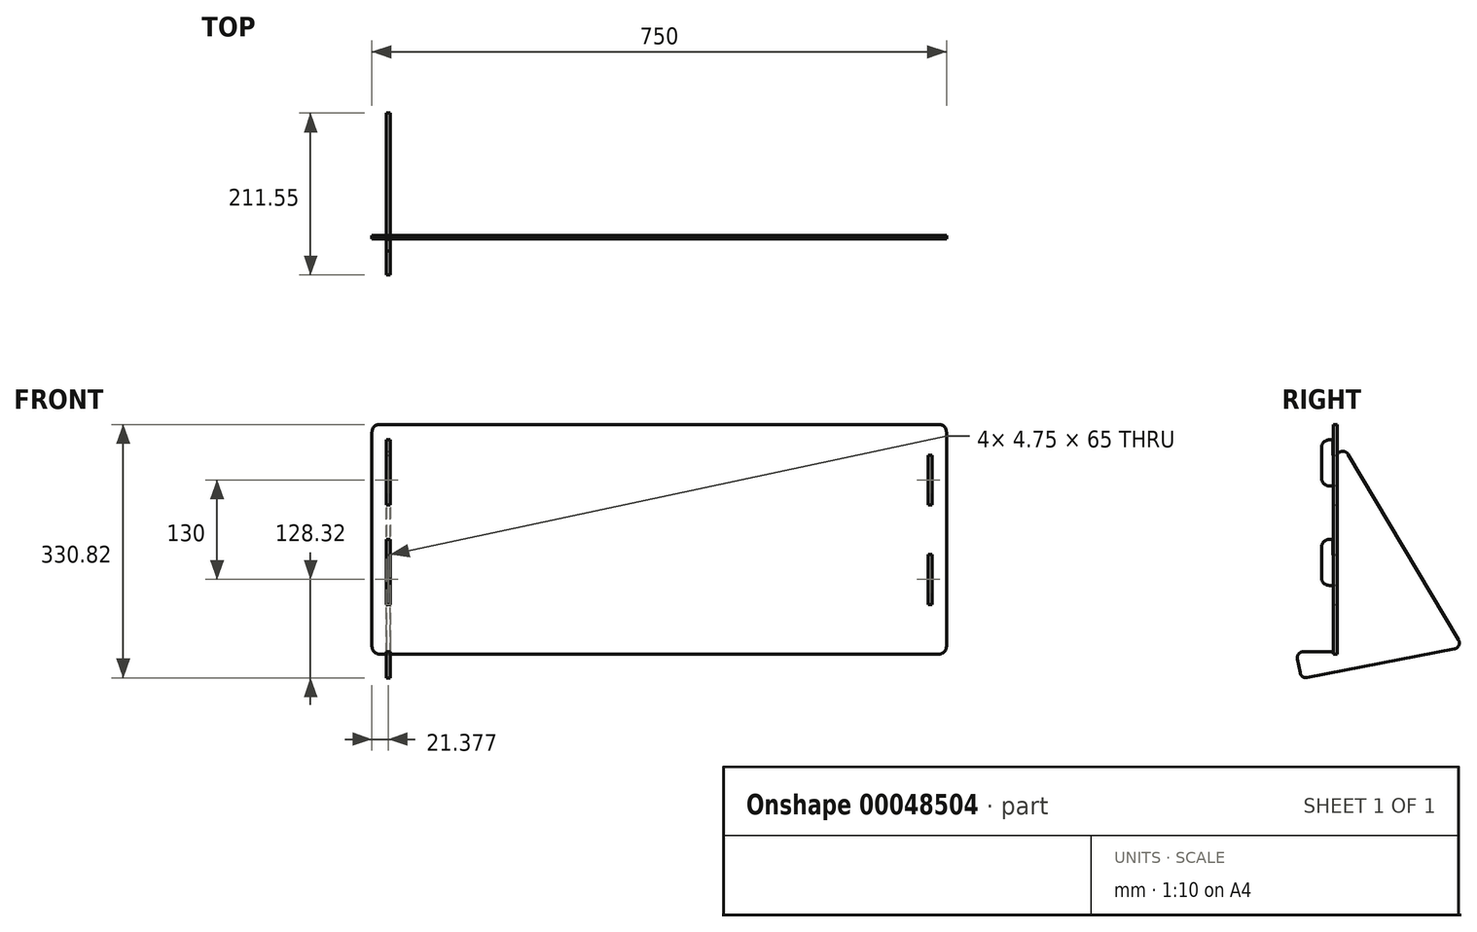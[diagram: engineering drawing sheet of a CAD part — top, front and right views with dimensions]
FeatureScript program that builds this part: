
annotation { "Feature Type Name" : "Feature", "Feature Type Description" : "" }
export const myFeature = defineFeature(function(context is Context, id is Id, definition is map)
    precondition{}
    {
        {
            assignVariable(context, id + "F0", {"name" : "thick", "anyValue" : 4.75});
        }
        {
            var Q0;
            Q0=qCreatedBy(makeId("Front.planeOp"),FACE);
            var sketch = newSketch(context, id + "F1", { "sketchPlane" : qUnion([Q0])});
            skLineSegment(sketch, "E0.bottom", {"start": v(-809.9, 170) * mm, "end": v(-59.9, 170) * mm});
            skLineSegment(sketch, "E0.top", {"start": v(-809.9, -130) * mm, "end": v(-59.9, -130) * mm});
            skLineSegment(sketch, "E0.left", {"start": v(-809.9, 170) * mm, "end": v(-809.9, -130) * mm});
            skLineSegment(sketch, "E0.right", {"start": v(-59.9, 170) * mm, "end": v(-59.9, -130) * mm});
            skLineSegment(sketch, "E1.bottom", {"start": v(-790.9, 130) * mm, "end": v(-786.16, 130) * mm});
            skLineSegment(sketch, "E1.top", {"start": v(-790.9, 65) * mm, "end": v(-786.16, 65) * mm});
            skLineSegment(sketch, "E1.left", {"start": v(-790.9, 130) * mm, "end": v(-790.9, 65) * mm});
            skLineSegment(sketch, "E1.right", {"start": v(-786.16, 130) * mm, "end": v(-786.16, 65) * mm});
            skLineSegment(sketch, "E2.bottom", {"start": v(-790.9, 0) * mm, "end": v(-786.16, 0) * mm});
            skLineSegment(sketch, "E2.top", {"start": v(-790.9, -65) * mm, "end": v(-786.16, -65) * mm});
            skLineSegment(sketch, "E2.left", {"start": v(-790.9, 0) * mm, "end": v(-790.9, -65) * mm});
            skLineSegment(sketch, "E2.right", {"start": v(-786.16, 0) * mm, "end": v(-786.16, -65) * mm});
            skLineSegment(sketch, "E3", {"start": v(-434.9, 170) * mm, "end": v(-434.9, -130) * mm, "construction": true});
            skLineSegment(sketch, "E4.MirrorCS", {"start": v(-78.9, -65) * mm, "end": v(-83.66, -65) * mm});
            skLineSegment(sketch, "E5.MirrorCS", {"start": v(-78.9, 65) * mm, "end": v(-83.66, 65) * mm});
            skLineSegment(sketch, "E6.MirrorCS", {"start": v(-78.9, 130) * mm, "end": v(-83.66, 130) * mm});
            skLineSegment(sketch, "E7.MirrorCS", {"start": v(-78.9, 0) * mm, "end": v(-83.66, 0) * mm});
            skLineSegment(sketch, "E8.MirrorCS", {"start": v(-78.9, 0) * mm, "end": v(-78.9, -65) * mm});
            skLineSegment(sketch, "E9.MirrorCS", {"start": v(-83.66, 130) * mm, "end": v(-83.66, 65) * mm});
            skLineSegment(sketch, "E10.MirrorCS", {"start": v(-78.9, 130) * mm, "end": v(-78.9, 65) * mm});
            skLineSegment(sketch, "E11.MirrorCS", {"start": v(-83.66, 0) * mm, "end": v(-83.66, -65) * mm});
            skSolve(sketch);
        }
        {
            var Q0;
            Q0=makeQuery(id+"F1.imprint","IMPRINT",FACE,{"disambiguationData":[TD([[makeQuery(id+"F1.imprint","IMPRINT",EDGE,{"derivedFrom":sQuery(id+"F1.wireOp",EDGE,"E0.bottom")}),-1.0]])]});
            extrude(context, id + "F2", {"entities" : qUnion([Q0]), "depth" : (getVariable(context, 'thick')) * mm});
        }
        {
            var Q0;
            Q0=makeQuery(id+"F2.opExtrude","SWEPT_FACE",FACE,{"disambiguationData":[OSD([sQuery(id+"F1.wireOp",EDGE,"E1.right")])]});
            var sketch = newSketch(context, id + "F3", { "sketchPlane" : qUnion([Q0])});
            skLineSegment(sketch, "E12", {"start": v(5.25, 149.79) * mm, "end": v(5.25, 129.79) * mm});
            skLineSegment(sketch, "E13", {"start": v(5.25, 129.79) * mm, "end": v(0, 129.79) * mm});
            skLineSegment(sketch, "E14", {"start": v(0, 129.79) * mm, "end": v(0, 155.14) * mm});
            skLineSegment(sketch, "E15", {"start": v(0, 155.14) * mm, "end": v(-164.33, -121.03) * mm});
            skLineSegment(sketch, "E16", {"start": v(0, -130.21) * mm, "end": v(0, -40.21) * mm});
            skLineSegment(sketch, "E17", {"start": v(0, -40.21) * mm, "end": v(20.25, -40.21) * mm});
            skLineSegment(sketch, "E18", {"start": v(20.25, -40.21) * mm, "end": v(20.25, 19.79) * mm});
            skLineSegment(sketch, "E19", {"start": v(5.25, 19.79) * mm, "end": v(20.25, 19.79) * mm});
            skLineSegment(sketch, "E20", {"start": v(5.25, 19.79) * mm, "end": v(5.25, -0.21) * mm});
            skLineSegment(sketch, "E21", {"start": v(5.25, -0.21) * mm, "end": v(0, -0.21) * mm});
            skLineSegment(sketch, "E22", {"start": v(0, -0.21) * mm, "end": v(0, 89.79) * mm});
            skLineSegment(sketch, "E23", {"start": v(0, 89.79) * mm, "end": v(20.25, 89.79) * mm});
            skLineSegment(sketch, "E24", {"start": v(20.25, 89.79) * mm, "end": v(20.25, 149.79) * mm});
            skLineSegment(sketch, "E25", {"start": v(20.25, 149.79) * mm, "end": v(5.25, 149.79) * mm});
            skLineSegment(sketch, "E26", {"start": v(-164.33, -121.03) * mm, "end": v(46.7, -162.2) * mm});
            skLineSegment(sketch, "E27", {"start": v(46.7, -162.2) * mm, "end": v(53.62, -126.76) * mm});
            skLineSegment(sketch, "E28", {"start": v(53.62, -126.76) * mm, "end": v(4.75, -126.76) * mm});
            skLineSegment(sketch, "E29", {"start": v(4.75, -126.76) * mm, "end": v(4.75, -130.21) * mm});
            skLineSegment(sketch, "E30", {"start": v(0, -130.21) * mm, "end": v(4.75, -130.21) * mm});
            skSolve(sketch);
        }
        {
            var Q0;
            Q0 = qSketchRegion(id + "F3", true);
            extrude(context, id + "F4", {"entities" : qUnion([Q0]), "depth" : (getVariable(context, 'thick')) * mm});
        }
        {
            var Q0;
            Q0=makeQuery(id+"F4.opExtrude","SWEPT_EDGE",EDGE,{"disambiguationData":[OSD([sQuery(id+"F3.wireOp",EDGE,"E24"),sQuery(id+"F3.wireOp",EDGE,"E25")])]});
            var Q1;
            Q1=makeQuery(id+"F4.opExtrude","SWEPT_EDGE",EDGE,{"disambiguationData":[OSD([sQuery(id+"F3.wireOp",EDGE,"E23"),sQuery(id+"F3.wireOp",EDGE,"E24")])]});
            var Q2;
            Q2=makeQuery(id+"F4.opExtrude","SWEPT_EDGE",EDGE,{"disambiguationData":[OSD([sQuery(id+"F3.wireOp",EDGE,"E18"),sQuery(id+"F3.wireOp",EDGE,"E19")])]});
            var Q3;
            Q3=makeQuery(id+"F4.opExtrude","SWEPT_EDGE",EDGE,{"disambiguationData":[OSD([sQuery(id+"F3.wireOp",EDGE,"E17"),sQuery(id+"F3.wireOp",EDGE,"E18")])]});
            var Q4;
            Q4=makeQuery(id+"F2.opExtrude","SWEPT_EDGE",EDGE,{"disambiguationData":[OSD([sQuery(id+"F1.wireOp",EDGE,"E0.bottom"),sQuery(id+"F1.wireOp",EDGE,"E0.left")])]});
            var Q5;
            Q5=makeQuery(id+"F2.opExtrude","SWEPT_EDGE",EDGE,{"disambiguationData":[OSD([sQuery(id+"F1.wireOp",EDGE,"E0.top"),sQuery(id+"F1.wireOp",EDGE,"E0.left")])]});
            var Q6;
            Q6=makeQuery(id+"F2.opExtrude","SWEPT_EDGE",EDGE,{"disambiguationData":[OSD([sQuery(id+"F1.wireOp",EDGE,"E0.bottom"),sQuery(id+"F1.wireOp",EDGE,"E0.right")])]});
            var Q7;
            Q7=makeQuery(id+"F2.opExtrude","SWEPT_EDGE",EDGE,{"disambiguationData":[OSD([sQuery(id+"F1.wireOp",EDGE,"E0.top"),sQuery(id+"F1.wireOp",EDGE,"E0.right")])]});
            fillet(context, id + "F5", {"entities" : qUnion([Q0, Q1, Q2, Q3, Q4, Q5, Q6, Q7]), "radius" : 10 * mm, "tangentPropagation" : true, "allowEdgeOverflow" : false});
        }
        {
            var Q0;
            Q0=makeQuery(id+"F4.opExtrude","SWEPT_EDGE",EDGE,{"disambiguationData":[OSD([sQuery(id+"F3.wireOp",EDGE,"E14"),sQuery(id+"F3.wireOp",EDGE,"E15")])]});
            var Q1;
            Q1=makeQuery(id+"F4.opExtrude","SWEPT_EDGE",EDGE,{"disambiguationData":[OSD([sQuery(id+"F3.wireOp",EDGE,"E15"),sQuery(id+"F3.wireOp",EDGE,"f447051a-51f3-4c33-9bca-5e57847a07c1")])]});
            var Q2;
            Q2=makeQuery(id+"F4.opExtrude","SWEPT_EDGE",EDGE,{"disambiguationData":[OSD([sQuery(id+"F3.wireOp",EDGE,"E27"),sQuery(id+"F3.wireOp",EDGE,"E28")])]});
            var Q3;
            Q3=makeQuery(id+"F4.opExtrude","SWEPT_EDGE",EDGE,{"disambiguationData":[OSD([sQuery(id+"F3.wireOp",EDGE,"E26"),sQuery(id+"F3.wireOp",EDGE,"E27")])]});
            fillet(context, id + "F6", {"entities" : qUnion([Q0, Q1, Q2, Q3]), "radius" : 8 * mm, "tangentPropagation" : true, "allowEdgeOverflow" : false});
        }
    });
